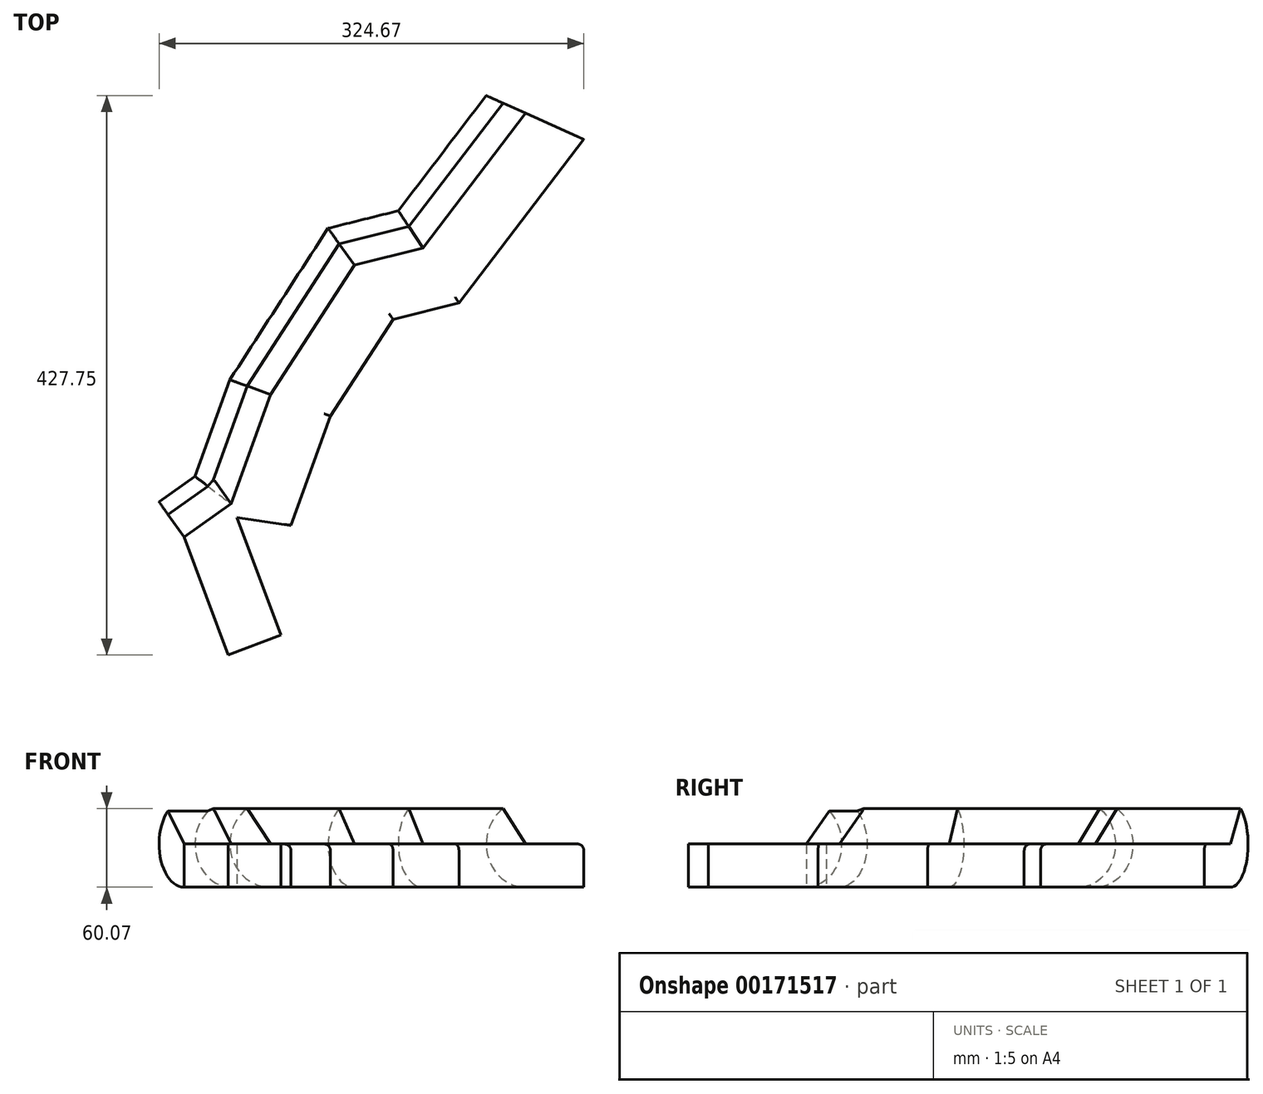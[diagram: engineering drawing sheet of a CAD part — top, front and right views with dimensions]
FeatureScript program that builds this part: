
annotation { "Feature Type Name" : "Feature", "Feature Type Description" : "" }
export const myFeature = defineFeature(function(context is Context, id is Id, definition is map)
    precondition{}
    {
        {
            var Q0;
            Q0=qCreatedBy(makeId("Top.planeOp"),FACE);
            var sketch = newSketch(context, id + "F0", { "sketchPlane" : qUnion([Q0])});
            skLineSegment(sketch, "E0", {"start": v(-52.4, 16.97) * mm, "end": v(-16.48, 42.46) * mm});
            skLineSegment(sketch, "E1", {"start": v(-16.48, 42.46) * mm, "end": v(29.36, 25.95) * mm});
            skLineSegment(sketch, "E2", {"start": v(29.36, 25.95) * mm, "end": v(-12.05, 32.11) * mm});
            skLineSegment(sketch, "E3", {"start": v(-12.05, 32.11) * mm, "end": v(-52.4, 16.97) * mm});
            skSolve(sketch);
        }
        {
            var Q0;
            Q0=makeQuery(id+"F0.imprint","IMPRINT",FACE,{"disambiguationData":[TD([[makeQuery(id+"F0.imprint","IMPRINT",EDGE,{"derivedFrom":sQuery(id+"F0.wireOp",EDGE,"E0")}),-1.0]])]});
            extrude(context, id + "F1", {"entities" : qUnion([Q0]), "depth" : 33.02 * mm});
        }
        {
            var Q0;
            Q0=makeQuery(id+"F1.opExtrude","SWEPT_FACE",FACE,{"disambiguationData":[OSD([sQuery(id+"F0.wireOp",EDGE,"E3")])]});
            extrude(context, id + "F2", {"entities" : qUnion([Q0]), "operationType" : NewBodyOperationType.ADD, "depth" : 96.27 * mm});
        }
        {
            var Q0;
            Q0=makeQuery(id+"F1.opExtrude","SWEPT_FACE",FACE,{"disambiguationData":[OSD([sQuery(id+"F0.wireOp",EDGE,"E1")])]});
            extrude(context, id + "F3", {"entities" : qUnion([Q0]), "operationType" : NewBodyOperationType.ADD, "depth" : 88.9 * mm});
        }
        {
            var Q0;
            Q0=makeQuery(id+"F3.opExtrude","SWEPT_FACE",FACE,{"disambiguationData":[OSD([sQuery(id+"F0.wireOp",EDGE,"E0"),sQuery(id+"F0.wireOp",EDGE,"E1")])]});
            var Q1;
            {var subQ0=sQuery(id+"F0.wireOp",EDGE,"E1");var subQ1=sQuery(id+"F0.wireOp",EDGE,"E0");Q1=makeQuery(id+"F3.opExtrude","SWEPT_EDGE",EDGE,{"disambiguationData":[OSD([subQ1,subQ0]),TDD([makeQuery(id+"F1.opExtrude","CAP_VERTEX",VERTEX,{"disambiguationData":[OSD([subQ1,subQ0])],"isStart":false})])]});}
            revolve(context, id + "F4", {"operationType" : NewBodyOperationType.ADD, "entities" : qUnion([Q0]), "axis" : qUnion([Q1]), "revolveType" : RevolveType.ONE_DIRECTION, "oppositeDirection" : true, "angle" : 145 * degree});
        }
        {
            var Q0;
            Q0=makeQuery(id+"F1.opExtrude","SWEPT_FACE",FACE,{"disambiguationData":[OSD([sQuery(id+"F0.wireOp",EDGE,"E0")])]});
            var Q1;
            Q1=makeQuery(id+"F1.opExtrude","CAP_EDGE",EDGE,{"disambiguationData":[OSD([sQuery(id+"F0.wireOp",EDGE,"E0")])],"isStart":false});
            revolve(context, id + "F5", {"operationType" : NewBodyOperationType.ADD, "entities" : qUnion([Q0]), "axis" : qUnion([Q1]), "revolveType" : RevolveType.ONE_DIRECTION, "angle" : 140 * degree});
        }
        {
            var Q0;
            {var subQ0=sQuery(id+"F0.wireOp",EDGE,"E1");var subQ1=sQuery(id+"F0.wireOp",EDGE,"E0");var subQ2=makeQuery(id+"F1.opExtrude","CAP_VERTEX",VERTEX,{"disambiguationData":[OSD([subQ1,subQ0])],"isStart":false});var subQ3=makeQuery(id+"F3.boolean.opBoolean","MERGE",VERTEX,{"derivedFrom":[subQ2,makeQuery(id+"F3.opExtrude","CAP_VERTEX",VERTEX,{"disambiguationData":[OSD([subQ1,subQ0]),TDD([subQ2])],"isStart":true})]});var subQ4=makeQuery(id+"F4.boolean.opBoolean","MERGE",VERTEX,{"derivedFrom":[subQ3,makeQuery(id+"F4.opRevolve","CAP_VERTEX",VERTEX,{"disambiguationData":[OSD([subQ1,subQ0]),TDD([subQ3])],"isStart":true})]});Q0=makeQuery(id+"F5.boolean.opBoolean","MERGE",VERTEX,{"derivedFrom":[subQ4,makeQuery(id+"F5.opRevolve","CAP_VERTEX",VERTEX,{"disambiguationData":[OSD([subQ1,subQ0]),TDD([subQ4])],"isStart":true})]});}
            var Q1;
            {var subQ0=sQuery(id+"F0.wireOp",EDGE,"E3");var subQ1=sQuery(id+"F0.wireOp",EDGE,"E0");var subQ2=makeQuery(id+"F1.opExtrude","CAP_VERTEX",VERTEX,{"disambiguationData":[OSD([subQ1,subQ0])],"isStart":false});var subQ3=makeQuery(id+"F2.boolean.opBoolean","MERGE",VERTEX,{"derivedFrom":[subQ2,makeQuery(id+"F2.opExtrude","CAP_VERTEX",VERTEX,{"disambiguationData":[OSD([subQ1,subQ0]),TDD([subQ2])],"isStart":true})]});Q1=makeQuery(id+"F5.boolean.opBoolean","MERGE",VERTEX,{"derivedFrom":[subQ3,makeQuery(id+"F5.opRevolve","CAP_VERTEX",VERTEX,{"disambiguationData":[OSD([subQ1,subQ0]),TDD([subQ3])],"isStart":true})]});}
            var Q2;
            Q2=makeQuery(id+"F5.opRevolve","CAP_VERTEX",VERTEX,{"disambiguationData":[OSD([sQuery(id+"F0.wireOp",EDGE,"E0"),sQuery(id+"F0.wireOp",EDGE,"E3")])],"isStart":false});
            cPlane(context, id + "F6", {"entities" : qUnion([Q0, Q1, Q2]), "cplaneType" : CPlaneType.THREE_POINT, "offset" : 25.4 * mm, "width" : 152.4 * mm, "height" : 152.4 * mm});
        }
        {
            var Q0;
            Q0=qCreatedBy(id+"F6.planeOp",FACE);
            var sketch = newSketch(context, id + "F7", { "sketchPlane" : qUnion([Q0])});
            skLineSegment(sketch, "E4", {"start": v(-52.17, 35.17) * mm, "end": v(-11.68, 53.65) * mm});
            skLineSegment(sketch, "E5", {"start": v(-11.68, 53.65) * mm, "end": v(-27.46, 88.24) * mm});
            skLineSegment(sketch, "E6", {"start": v(-27.46, 88.24) * mm, "end": v(-69.48, 69.06) * mm});
            skLineSegment(sketch, "E7", {"start": v(-69.48, 69.06) * mm, "end": v(-52.17, 35.17) * mm});
            skSolve(sketch);
        }
        {
            var Q0;
            Q0=makeQuery(id+"F7.imprint","IMPRINT",FACE,{"disambiguationData":[TD([[makeQuery(id+"F7.imprint","IMPRINT",EDGE,{"derivedFrom":sQuery(id+"F7.wireOp",EDGE,"E4")}),1.0]])]});
            extrude(context, id + "F8", {"entities" : qUnion([Q0]), "operationType" : NewBodyOperationType.REMOVE, "depth" : 15 * mm});
        }
        {
            var Q0;
            {var subQ0=sQuery(id+"F0.wireOp",EDGE,"E2");var subQ1=sQuery(id+"F0.wireOp",EDGE,"E1");Q0=makeQuery(id+"F3.opExtrude","SWEPT_EDGE",EDGE,{"disambiguationData":[OSD([subQ1,subQ0]),TDD([makeQuery(id+"F1.opExtrude","CAP_VERTEX",VERTEX,{"disambiguationData":[OSD([subQ1,subQ0])],"isStart":false})])]});}
            fillet(context, id + "F9", {"entities" : qUnion([Q0]), "radius" : 5.08 * mm, "tangentPropagation" : true, "allowEdgeOverflow" : false});
        }
        {
            var Q0;
            {var subQ0=sQuery(id+"F0.wireOp",EDGE,"E1");var subQ1=sQuery(id+"F0.wireOp",EDGE,"E3");Q0=makeQuery(id+"F3.boolean.opBoolean","MERGE",FACE,{"derivedFrom":[makeQuery(id+"F2.boolean.opBoolean","MERGE",FACE,{"derivedFrom":[makeQuery(id+"F1.opExtrude","CAP_FACE",FACE,{"disambiguationData":[OSD([sQuery(id+"F0.wireOp",EDGE,"E0"),subQ0,sQuery(id+"F0.wireOp",EDGE,"E2"),subQ1])],"isStart":false}),makeQuery(id+"F2.opExtrude","SWEPT_FACE",FACE,{"disambiguationData":[OSD([subQ1]),TDD([makeQuery(id+"F1.opExtrude","CAP_EDGE",EDGE,{"disambiguationData":[OSD([subQ1])],"isStart":false})])]})]}),makeQuery(id+"F3.opExtrude","SWEPT_FACE",FACE,{"disambiguationData":[OSD([subQ0]),TDD([makeQuery(id+"F1.opExtrude","CAP_EDGE",EDGE,{"disambiguationData":[OSD([subQ0])],"isStart":false})])]})]});}
            var sketch = newSketch(context, id + "F10", { "sketchPlane" : qUnion([Q0])});
            skLineSegment(sketch, "E8", {"start": v(13.64, 126.1) * mm, "end": v(77.77, 225) * mm});
            skLineSegment(sketch, "E9", {"start": v(77.77, 225) * mm, "end": v(130.1, 238.05) * mm});
            skLineSegment(sketch, "E10", {"start": v(130.1, 238.05) * mm, "end": v(208.71, 341.05) * mm});
            skSolve(sketch);
        }
        {
            var Q0;
            {var subQ0=sQuery(id+"F0.wireOp",EDGE,"E1");var subQ1=sQuery(id+"F0.wireOp",EDGE,"E0");Q0=makeQuery(id+"F4.boolean.opBoolean","MERGE",FACE,{"derivedFrom":[makeQuery(id+"F3.opExtrude","CAP_FACE",FACE,{"disambiguationData":[OSD([subQ0])],"isStart":false}),makeQuery(id+"F4.opRevolve","SWEPT_FACE",FACE,{"disambiguationData":[OSD([subQ1,subQ0]),TDD([makeQuery(id+"F3.opExtrude","CAP_EDGE",EDGE,{"disambiguationData":[OSD([subQ1,subQ0])],"isStart":false})])]})]});}
            var Q1;
            Q1 = qConstructionFilter(qBodyType(qCreatedBy(id + "F10" ,EDGE), BodyType.WIRE), ConstructionObject.NO);
            sweep(context, id + "F11", {"operationType" : NewBodyOperationType.ADD, "profiles" : qUnion([Q0]), "path" : qUnion([Q1])});
        }
    });
